FCSTD DOCUMENT  (FreeCAD 1.0RUnknown)
Label: collectionDrawing
License: All rights reserved
objects: TechDraw::DrawViewDimension×3, TechDraw::DrawProjGroupItem×2, App::Link×1, Spreadsheet::Sheet×1, TechDraw::DrawSVGTemplate×1, TechDraw::DrawViewSpreadsheet×1, TechDraw::DrawPage×1
note: 3 computed .brp shape members not serialized (recipe doc carries the construction recipe); baked Part::Feature solids carry a one-line shape summary decoded from their .brp
EXTERNAL_REF file=subassemblies/parts/wardrobe_base_jan.FCStd obj=Body
EXTERNAL_REF file=mastersheet.FCStd obj=Spreadsheet
EXTERNAL_REF file=mastersketch.FCStd obj=Sketch
EXTERNAL_REF file=mastersketch.FCStd obj=Sketch001
EXTERNAL_REF file=mastersketch.FCStd obj=Spreadsheet
EXTERNAL_REF file=subassemblies/parts/wardrobe_left_corpus03_jan.FCStd obj=Sketch
EXTERNAL_REF file=subassemblies/parts/wardrobe_top_corpus03_jan.FCStd obj=Sketch

FEATURE [App::Link] Link
  LinkedObject = -> <external subassemblies/parts/wardrobe_base_jan.FCStd>#Body
FEATURE [Spreadsheet::Sheet] Spreadsheet
  cells = A1='Benennung; B1='A: Länge [mm]; C1='B: Breite [mm]; D1='C: Stärke [mm]; E1='Anzahl; F1='Material; G1='Umleimung; H1='€/m²; I1='€; J1='Artikelnr. Hornbach; A2='Seitenteile Korpus 1; B2==mastersketch#Spreadsheet.corpus_height - 2 * mastersketch#Spreadsheet.corpus_outer_thickness; C2==mastersketch#Spreadsheet.corpus_depth; D2==mastersketch#Spreadsheet.corpus_outer_thickness; E2=2; G2='d; e; g; H2=18.95; I2==B2 * C2 / 10 ^ 6 * H2 * E2; J2=12391882; A3='Seitenteile Korpus 2; B3==mastersketch#Spreadsheet.corpus01_height - 2 * mastersketch#Spreadsheet.corpus_outer_thickness; C3==mastersketch#Spreadsheet.corpus_depth; D3==mastersketch#Spreadsheet.corpus_outer_thickness; E3=2; G3='d; e; g; H3=18.95; I3==B3 * C3 / 10 ^ 6 * H3 * E3; J3=12391882; A4='Seitenteile Korpus 3; B4==mastersketch#Spreadsheet.corpus02_height - 2 * mastersketch#Spreadsheet.corpus_outer_thickness; C4==mastersketch#Spreadsheet.corpus_depth; D4==mastersketch#Spreadsheet.corpus_outer_thickness; E4=2; G4='d; e; g; H4=18.95; I4==B4 * C4 / 10 ^ 6 * H4 * E4; J4=12391882; A5='Linkes Seitenteil Korpus 4 (Rohabmaße, Genau: Zgn:33); B5==mastersketch#Spreadsheet.corpus_depth; C5==wardrobe_left_corpus03_jan#Sketch.Constraints.max_height / 1 mm; D5==mastersketch#Spreadsheet.corpus_outer_thickness; E5=1; G5='d; g; H5=18.95; I5==B5 * C5 / 10 ^ 6 * H5 * E5; J5=12391882; A6='Rechtes Seitenteil Korpus 4 (Rohabmaße, Genau: Zgn:34); B6==mastersketch#Spreadsheet.corpus_depth; C6==mastersketch#<<corpus>>.Constraints.corpus03_right_height / 1 mm; D6==mastersketch#Spreadsheet.corpus_outer_thickness; E6=1; G6='d; g; H6=18.95; I6==B6 * C6 / 10 ^ 6 * H6 * E6; J6=12391882; A7='Deckplatten Korpus 1-3; B7==mastersketch#Spreadsheet.corpus_depth; C7==mastersketch#Spreadsheet.corpus_width; D7==mastersketch#Spreadsheet.corpus_outer_thickness; E7=3; G7='g; d; f; H7=18.95; I7==B7 * C7 / 10 ^ 6 * H7 * E7; J7=12391882; A8='Deckplatte Korpus 4 (Rohabmaße, Genau: Zgn:23); B8==mastersketch#Spreadsheet.corpus_depth; C8==wardrobe_top_corpus03_jan#Sketch.Constraints.max_length / 1 mm; D8==mastersketch#Spreadsheet.corpus_outer_thickness; E8=1; G8='g; d; f; H8=18.95; I8==B8 * C8 / 10 ^ 6 * H8 * E8; J8=12391882; A9='Grundplatten Korpus 1-3; B9==mastersketch#Spreadsheet.corpus_depth; C9==mastersketch#Spreadsheet.corpus_width; D9==mastersketch#Spreadsheet.corpus_outer_thickness; E9=3; G9='g; d; f; H9=18.95; I9==B9 * C9 / 10 ^ 6 * H9 * E9; J9=12391882; A10='Grundplatte Korpus 4; B10==mastersketch#Spreadsheet.corpus_depth; C10==mastersketch#<<corpus>>.Constraints.corpus03_width / 1 mm; D10==mastersketch#Spreadsheet.corpus_outer_thickness; E10=1; G10='g; d; f; H10=18.95; I10==B10 * C10 / 10 ^ 6 * H10 * E10; J10=12391882; A11='Rückplatte Korpus 1; B11==mastersketch#Spreadsheet.corpus_height; C11==mastersketch#Spreadsheet.corpus_width; D11==mastersketch#Spreadsheet.corpus_backplate_thickness; E11=1; H11=13.5; I11==B11 * C11 / 10 ^ 6 * H11 * E11; J11=10254585; A12='Rückplatte Korpus 2; B12==mastersketch#Spreadsheet.corpus01_height; C12==mastersketch#Spreadsheet.corpus_width; D12==mastersketch#Spreadsheet.corpus_backplate_thickness; E12=1; H12=13.5; I12==B12 * C12 / 10 ^ 6 * H12 * E12; J12=10254585; A13='Rückplatte Korpus 3; B13==mastersketch#Spreadsheet.corpus02_height; C13==mastersketch#Spreadsheet.corpus_width; D13==mastersketch#Spreadsheet.corpus_backplate_thickness; E13=1; H13=13.5; I13==B13 * C13 / 10 ^ 6 * H13 * E13; J13=10254585; A14='Rückplatte Korpus 4 (Rohabmaße, Genau: Zgn:30); B14==mastersketch#<<corpus>>.Constraints.corpus03_back_height / 1 mm; C14==mastersketch#<<corpus>>.Constraints.corpus03_width / 1 mm; D14==mastersketch#Spreadsheet.corpus_backplate_thickness; E14=1; H14=13.5; I14==B14 * C14 / 10 ^ 6 * H14 * E14; J14=10254585; A15='Schublade Seitenteile; B15==mastersketch#Spreadsheet.drawer_length - 2 * mastersketch#Spreadsheet.drawer_outer_thickness; C15=170; D15==mastersketch#Spreadsheet.drawer_outer_thickness; E15=24; G15='umlaufend; H15=18.95; I15==B15 * C15 / 10 ^ 6 * H15 * E15; J15=12391882; A16='Schublade Fronten; B16=477; C16==mastersketch#Spreadsheet.drawer_height; D16==mastersketch#Spreadsheet.drawer_outer_thickness; E16=12; G16='umlaufend; H16=18.95; I16==B16 * C16 / 10 ^ 6 * H16 * E16; J16=12391882; A17='Schublade Rückplatten; B17==mastersketch#Spreadsheet.drawer_width; C17==mastersketch#Spreadsheet.drawer_height - (mastersketch#Spreadsheet.drawer_bottom_thickness + mastersketch#Spreadsheet.drawer_bottom_tol + mastersketch#Spreadsheet.drawer_slot_height); D17==mastersketch#Spreadsheet.drawer_outer_thickness; E17=12; G17='umlaufend; H17=18.95; I17==B17 * C17 / 10 ^ 6 * H17 * E17; J17=12391882; A18='Schublade Einlegeboden; B18==mastersketch#Spreadsheet.drawer_width + 2 * (mastersketch#Spreadsheet.drawer_slot_depth + mastersketch#Spreadsheet.drawer_bottom_tol) - 2 * mastersketch#Spreadsheet.drawer_outer_thickness - 2; C18==mastersketch#Spreadsheet.drawer_length + mastersketch#Spreadsheet.drawer_slot_depth + mastersketch#Spreadsheet.drawer_bottom_tol - mastersketch#Spreadsheet.drawer_outer_thickness; D18==mastersketch#Spreadsheet.drawer_bottom_thickness; E18=12; H18=21.85; I18==B18 * C18 / 10 ^ 6 * H18 * E18; J18=5190651; A19='Tür Korpus 1 (Rohabmaße, Genau: Zgn:10); B19==mastersketch#Sketch.Constraints.corpus00_door_height / 1 mm; C19==mastersheet#Spreadsheet.corpus_width - 5; D19==mastersketch#Spreadsheet.corpus_outer_thickness; E19=1; G19='umlaufend; H19=18.95; I19==B19 * C19 / 10 ^ 6 * H19 * E19; J19=12391882; A20='Tür Korpus 2 (Rohabmaße, Genau: Zgn:11); B20==mastersketch#Sketch.Constraints.corpus01_door_height / 1 mm; C20==mastersheet#Spreadsheet.corpus_width - 5; D20==mastersketch#Spreadsheet.corpus_outer_thickness; E20=1; G20='umlaufend; H20=18.95; I20==B20 * C20 / 10 ^ 6 * H20 * E20; J20=12391882; A21='Tür Korpus 3 (Rohabmaße, Genau: Zgn:12); B21==mastersketch#Sketch.Constraints.corpus02_door_height / 1 mm; C21==mastersheet#Spreadsheet.corpus_width - 5; D21==mastersketch#Spreadsheet.corpus_outer_thickness; E21=1; G21='umlaufend; H21=18.95; I21==B21 * C21 / 10 ^ 6 * H21 * E21; J21=12391882; A22='Tür Korpus 4 (Rohabmaße, Genau: Zgn:13); B22==mastersketch#Sketch.Constraints.corpus03_door_height / 1 mm; C22==mastersketch#Sketch.Constraints.corpus03_door_width / 1 mm; D22==mastersketch#Spreadsheet.corpus_outer_thickness; E22=1; G22='umlaufend; H22=18.95; I22==B22 * C22 / 10 ^ 6 * H22 * E22; J22=12391882; H23='Summe; I23==sum(I2:I22); A24='Einzelteile:; A25='Benennnung; G25='€/stk; H25='Anzahl; +12 more cells
FEATURE [TechDraw::DrawSVGTemplate] Template001  label="Vorlage001"
  EditableTexts = AuthorName=Jan van de Locht; CheckDate=15.08.2025; CreationDate=15.08.2025; DrawingNumber=40; FC-Title=Übersichtszeichnung; SheetNumber=1 / 1; Subtitle=Korpus 1-4, Quadratische Platten; SupervisorName=Jan van de Locht; Weight=WEIGHT; scale=1 : 1
  Height = 297
  Orientation = 1
  Template = <userpath>/scoop/apps/freecad/current/data/Mod/TechDraw/Templates/A3_Landscape_TD.svg
  Width = 420
FEATURE [TechDraw::DrawProjGroupItem] View002
  CoarseView = false
  Direction = (0,-1,0)
  Focus = 100
  HardHidden = false
  IsoCount = 0
  IsoHidden = false
  IsoVisible = false
  LockPosition = false
  Perspective = false
  Rotation = 0
  RotationVector = (1,0,0)
  Scale = 0.2
  ScaleType = 2
  ScrubCount = 1
  SeamHidden = false
  SeamVisible = false
  SmoothHidden = false
  SmoothVisible = true
  Type = 0
  X = 335.01
  XDirection = (1,0,0)
  XSource = -> [Link]
  Y = 127.803
FEATURE [TechDraw::DrawProjGroupItem] View003
  CoarseView = false
  Direction = (0,0,-1)
  Focus = 100
  HardHidden = false
  IsoCount = 0
  IsoHidden = false
  IsoVisible = false
  LockPosition = false
  Perspective = false
  Rotation = 0
  RotationVector = (1,0,0)
  Scale = 0.2
  ScaleType = 2
  ScrubCount = 1
  SeamHidden = false
  SeamVisible = false
  SmoothHidden = false
  SmoothVisible = true
  Type = 0
  X = 335.01
  XDirection = (1,0,0)
  XSource = -> [Link]
  Y = 211.815
FEATURE [TechDraw::DrawViewSpreadsheet] Sheet001
  CellEnd = F22
  CellStart = A1
  Font = MS Shell Dlg 2
  LineWidth = 0.35
  LockPosition = false
  Rotation = 0
  ScaleType = 0
  Source = -> Spreadsheet
  Symbol = <blob: 28655 chars omitted>
  TextSize = 12
  X = 135.522
  Y = 199.306
FEATURE [TechDraw::DrawViewDimension] Dimension  label="Maß"
  AngleOverride = false
  Arbitrary = true
  ArbitraryTolerances = false
  BoxCorners = (2) [(-54,-60,0),(54,60,0)]
  EqualTolerance = true
  ExtensionAngle = 0
  FormatSpec = B
  FormatSpecOverTolerance = %+.1w
  FormatSpecUnderTolerance = %+.1w
  Inverted = false
  LineAngle = 0
  LockPosition = false
  MeasureType = 1
  OverTolerance = 0
  References2D = -> [View003]
  Rotation = 0
  ScaleType = 0
  TheoreticalExact = false
  Type = 1
  UnderTolerance = 0
  X = 0
  Y = -63.6112
FEATURE [TechDraw::DrawViewDimension] Dimension001  label="Maß001"
  AngleOverride = false
  Arbitrary = true
  ArbitraryTolerances = false
  BoxCorners = (2) [(-54,-60,0),(54,60,0)]
  EqualTolerance = true
  ExtensionAngle = 0
  FormatSpec = A
  FormatSpecOverTolerance = %+.1w
  FormatSpecUnderTolerance = %+.1w
  Inverted = false
  LineAngle = 0
  LockPosition = false
  MeasureType = 1
  OverTolerance = 0
  References2D = -> [View003]
  Rotation = 0
  ScaleType = 0
  TheoreticalExact = false
  Type = 2
  UnderTolerance = 0
  X = 56.84
  Y = -4.55552
FEATURE [TechDraw::DrawViewDimension] Dimension002  label="Maß002"
  AngleOverride = false
  Arbitrary = true
  ArbitraryTolerances = false
  BoxCorners = (2) [(-54,-1.9,0),(54,1.9,0)]
  EqualTolerance = true
  ExtensionAngle = 0
  FormatSpec = C
  FormatSpecOverTolerance = %+.1w
  FormatSpecUnderTolerance = %+.1w
  Inverted = false
  LineAngle = 0
  LockPosition = false
  MeasureType = 1
  OverTolerance = 0
  References2D = -> [View002]
  Rotation = 0
  ScaleType = 0
  TheoreticalExact = false
  Type = 0
  UnderTolerance = 0
  X = 57.6135
  Y = -9.96444
FEATURE [TechDraw::DrawPage] Page001  label="Seite001"
  KeepUpdated = true
  NextBalloonIndex = 1
  ProjectionType = 0
  Template = -> Template001
  Views = -> [View002,View003,Sheet001,Dimension,Dimension001,Dimension002]
